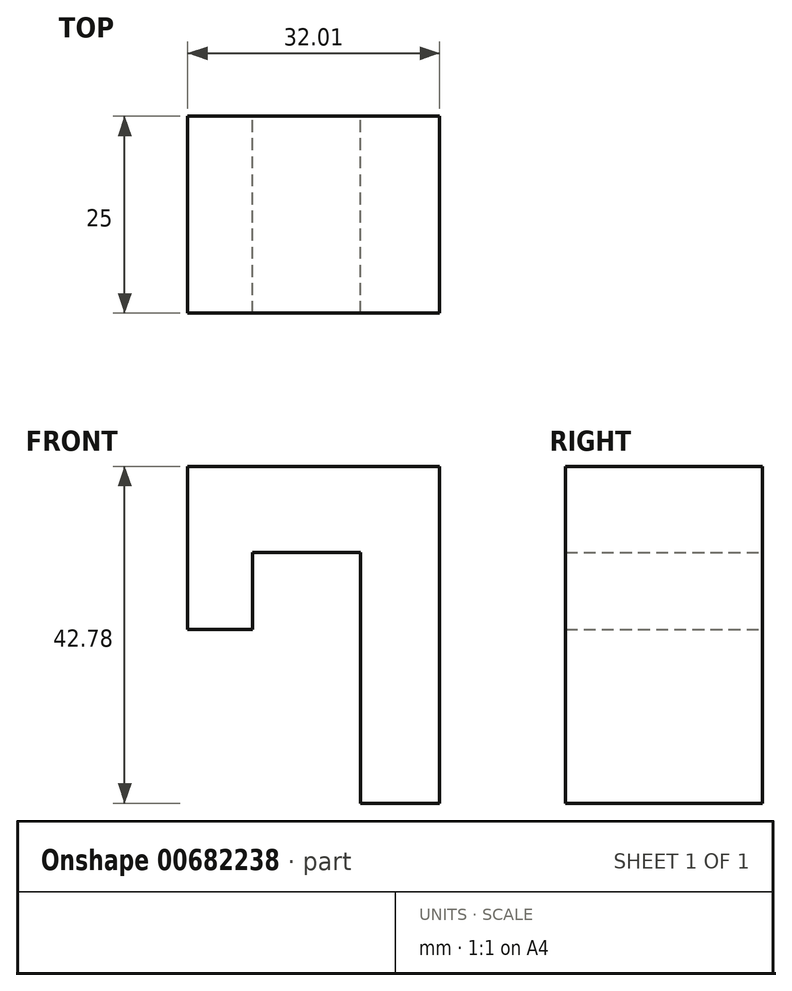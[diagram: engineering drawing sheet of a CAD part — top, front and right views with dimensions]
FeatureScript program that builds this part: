
annotation { "Feature Type Name" : "Feature", "Feature Type Description" : "" }
export const myFeature = defineFeature(function(context is Context, id is Id, definition is map)
    precondition{}
    {
        {
            var Q0;
            Q0=qCreatedBy(makeId("Front.planeOp"),FACE);
            var sketch = newSketch(context, id + "F0", { "sketchPlane" : qUnion([Q0])});
            skLineSegment(sketch, "E0", {"start": v(-21.95, -9.77) * mm, "end": v(-21.95, 10.9) * mm});
            skLineSegment(sketch, "E1", {"start": v(-21.95, 10.9) * mm, "end": v(10.06, 10.9) * mm});
            skLineSegment(sketch, "E2", {"start": v(10.06, 10.9) * mm, "end": v(10.06, -31.87) * mm});
            skLineSegment(sketch, "E3", {"start": v(0, 0) * mm, "end": v(0, -31.87) * mm});
            skLineSegment(sketch, "E4", {"start": v(0, -31.87) * mm, "end": v(10.06, -31.87) * mm});
            skLineSegment(sketch, "E5", {"start": v(-21.95, -9.77) * mm, "end": v(-13.7, -9.77) * mm});
            skLineSegment(sketch, "E6", {"start": v(-13.7, -9.77) * mm, "end": v(-13.7, 0) * mm});
            skLineSegment(sketch, "E7", {"start": v(-13.7, 0) * mm, "end": v(0, 0) * mm});
            skSolve(sketch);
        }
        {
            var Q0;
            Q0 = qSketchRegion(id + "F0", true);
            extrude(context, id + "F1", {"entities" : qUnion([Q0]), "depth" : 25 * mm, "offsetDistance" : 25 * mm});
        }
    });
